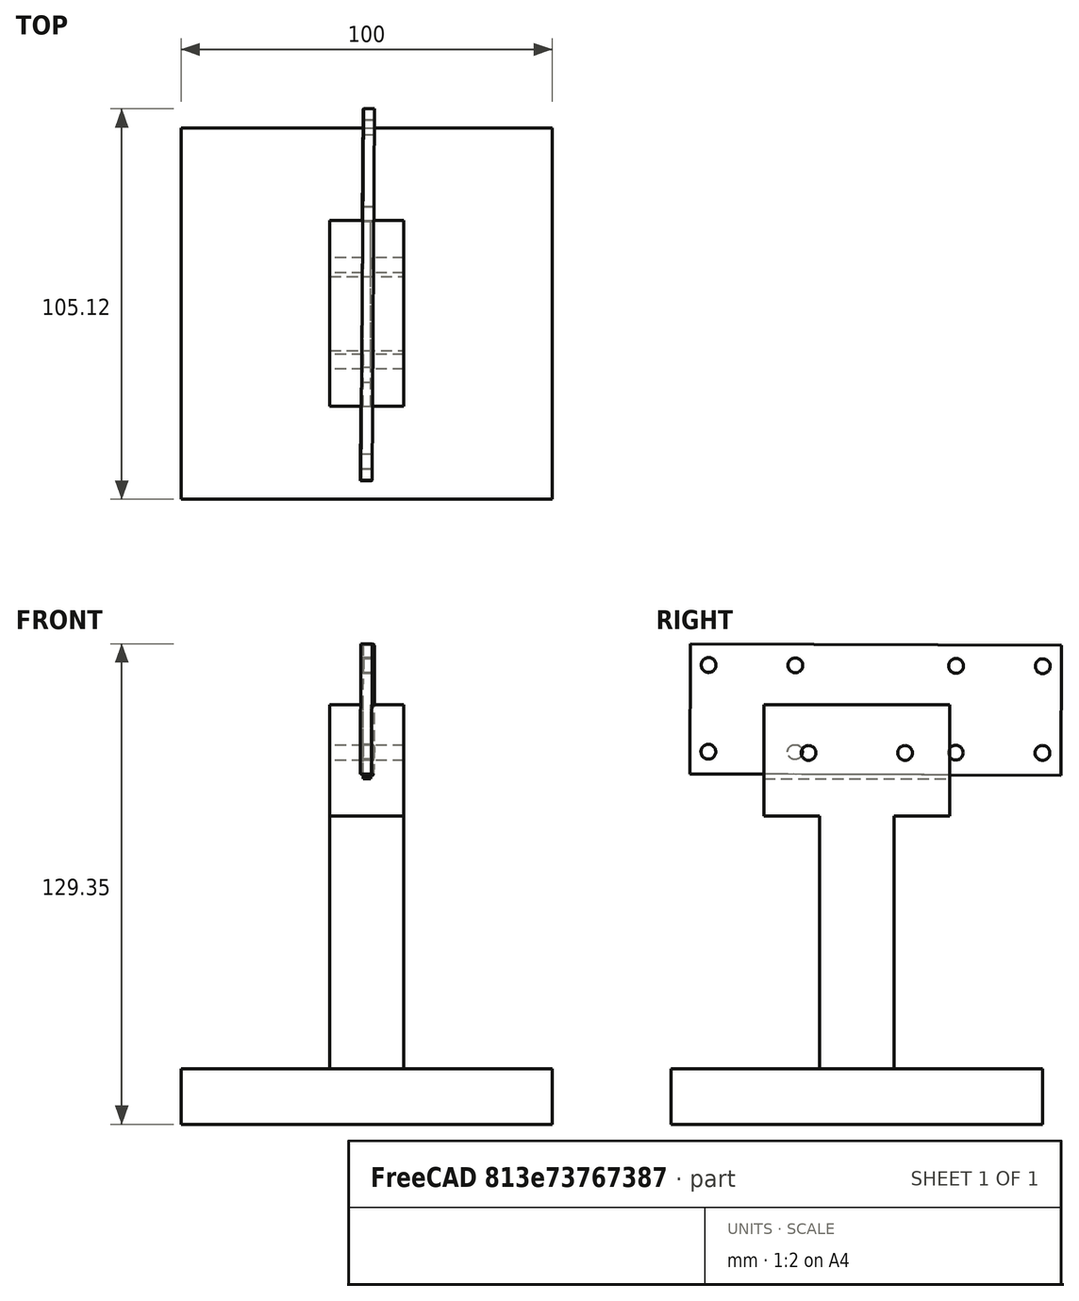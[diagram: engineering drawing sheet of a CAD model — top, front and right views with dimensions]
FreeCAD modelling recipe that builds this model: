
FCSTD DOCUMENT  (FreeCAD 0.16RUnknown)
Label: suporte_v0
License: All rights reserved
LicenseURL: http://en.wikipedia.org/wiki/All_rights_reserved
objects: Part::Cut×11, Part::Cylinder×10, Part::Box×5, Part::MultiFuse×2
note: 28 computed .brp shape members not serialized (recipe doc carries the construction recipe); baked Part::Feature solids carry a one-line shape summary decoded from their .brp

FEATURE [Part::Box] Box  label="Base"
  Height = 15
  Length = 100
  Width = 100
FEATURE [Part::Box] Box001  label="TroncoSolido"
  Height = 100
  Length = 20
  Placement = pos=(40,40,13) rot=(0,0,1;0rad)
  Width = 20
FEATURE [Part::Box] Box002  label="ChanfroTronco"
  Height = 30
  Length = 2
  Placement = pos=(49,25,93) rot=(0,0,1;0rad)
  Width = 50
FEATURE [Part::Cylinder] Cylinder
  Angle = 360
  Height = 10
  Radius = 2
FEATURE [Part::Cylinder] Cylinder001
  Angle = 360
  Height = 10
  Placement = pos=(23.35,0,0) rot=(0,0,1;0rad)
  Radius = 2
FEATURE [Part::Cylinder] Cylinder002
  Angle = 360
  Height = 10
  Placement = pos=(0,23.35,0) rot=(0,0,1;0rad)
  Radius = 2
FEATURE [Part::Cylinder] Cylinder003
  Angle = 360
  Height = 10
  Placement = pos=(23.35,23.35,0) rot=(0,0,1;0rad)
  Radius = 2
FEATURE [Part::Box] Box004  label="Cube"
  Height = 3
  Length = 100
  Placement = pos=(-5,-6,0) rot=(0,0,1;0rad)
  Width = 35
FEATURE [Part::Cut] Cut001
  Base = -> Box004
  Tool = -> Cylinder
FEATURE [Part::Cut] Cut002
  Base = -> Cut001
  Tool = -> Cylinder003
FEATURE [Part::Cut] Cut003
  Base = -> Cut002
  Tool = -> Cylinder001
FEATURE [Part::Cut] Cut004
  Base = -> Cut003
  Tool = -> Cylinder002
FEATURE [Part::Cylinder] Cylinder004
  Angle = 360
  Height = 10
  Placement = pos=(90,23.35,0) rot=(0,0,1;0rad)
  Radius = 2
FEATURE [Part::Cylinder] Cylinder005
  Angle = 360
  Height = 10
  Placement = pos=(90,0,0) rot=(0,0,1;0rad)
  Radius = 2
FEATURE [Part::Cylinder] Cylinder006
  Angle = 360
  Height = 10
  Placement = pos=(66.65,23.35,0) rot=(0,0,1;0rad)
  Radius = 2
FEATURE [Part::Cylinder] Cylinder007
  Angle = 360
  Height = 10
  Placement = pos=(66.65,0,0) rot=(0,0,1;0rad)
  Radius = 2
FEATURE [Part::Cut] Cut005
  Base = -> Cut004
  Tool = -> Cylinder004
FEATURE [Part::Cut] Cut006
  Base = -> Cut005
  Tool = -> Cylinder007
FEATURE [Part::Cut] Cut007
  Base = -> Cut006
  Tool = -> Cylinder006
FEATURE [Part::Cut] Cut008  label="Suporte_SemFurosCentrais"
  Base = -> Cut007
  Placement = pos=(52,100,100) rot=(-0.573216,0.579406,0.579406;4.18879rad)
  Tool = -> Cylinder005
FEATURE [Part::Box] Box005  label="T"
  Height = 30
  Length = 20
  Placement = pos=(40,25,83) rot=(0,0,1;0rad)
  Width = 50
FEATURE [Part::MultiFuse] Fusion  label="TroncoT"
  Shapes = -> [Box005,Box001]
FEATURE [Part::Cut] Cut  label="TroncoChanfro"
  Base = -> Fusion
  Tool = -> Box002
FEATURE [Part::Cylinder] Cylinder009  label="ParafusoTDir"
  Angle = 360
  Height = 25
  Placement = pos=(62.5,37,100) rot=(0,-1,0;1.5708rad)
  Radius = 2
FEATURE [Part::Cylinder] Cylinder010  label="ParafusoTEsq"
  Angle = 360
  Height = 25
  Placement = pos=(62.5,63,100) rot=(0,-1,0;1.5708rad)
  Radius = 2
FEATURE [Part::Cut] Cut009
  Base = -> Cut
  Tool = -> Cylinder009
FEATURE [Part::Cut] Cut010  label="TroncoTParafusos"
  Base = -> Cut009
  Tool = -> Cylinder010
FEATURE [Part::MultiFuse] Fusion001  label="Suporte_v0"
  Shapes = -> [Cut010,Box]
